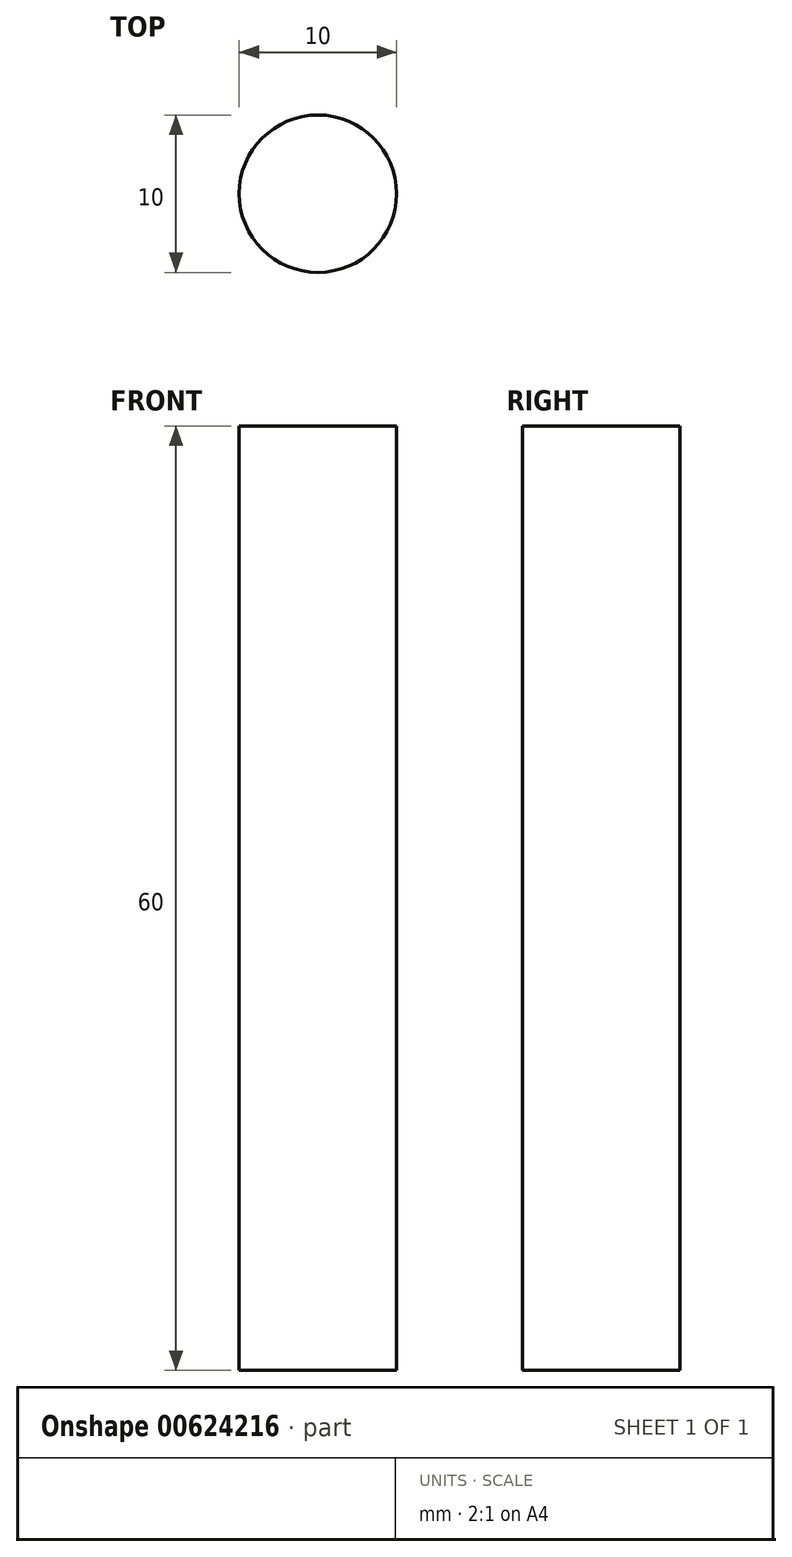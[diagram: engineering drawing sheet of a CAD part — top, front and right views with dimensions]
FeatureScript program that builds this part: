
annotation { "Feature Type Name" : "Feature", "Feature Type Description" : "" }
export const myFeature = defineFeature(function(context is Context, id is Id, definition is map)
    precondition{}
    {
        {
            var Q0;
            Q0=qCreatedBy(makeId("Top.planeOp"),FACE);
            var sketch = newSketch(context, id + "F0", { "sketchPlane" : qUnion([Q0])});
            skCircle(sketch, "E0", {"center": v(0, 0) * mm, "radius": 5 * mm});
            skSolve(sketch);
        }
        {
            var Q0;
            Q0=makeQuery(id+"F0.imprint","IMPRINT",FACE,{"disambiguationData":[TD([[makeQuery(id+"F0.imprint","IMPRINT",EDGE,{"derivedFrom":sQuery(id+"F0.wireOp",EDGE,"E0")}),1.0]])]});
            extrude(context, id + "F1", {"entities" : qUnion([Q0]), "depth" : 60 * mm, "offsetDistance" : 25 * mm});
        }
    });
